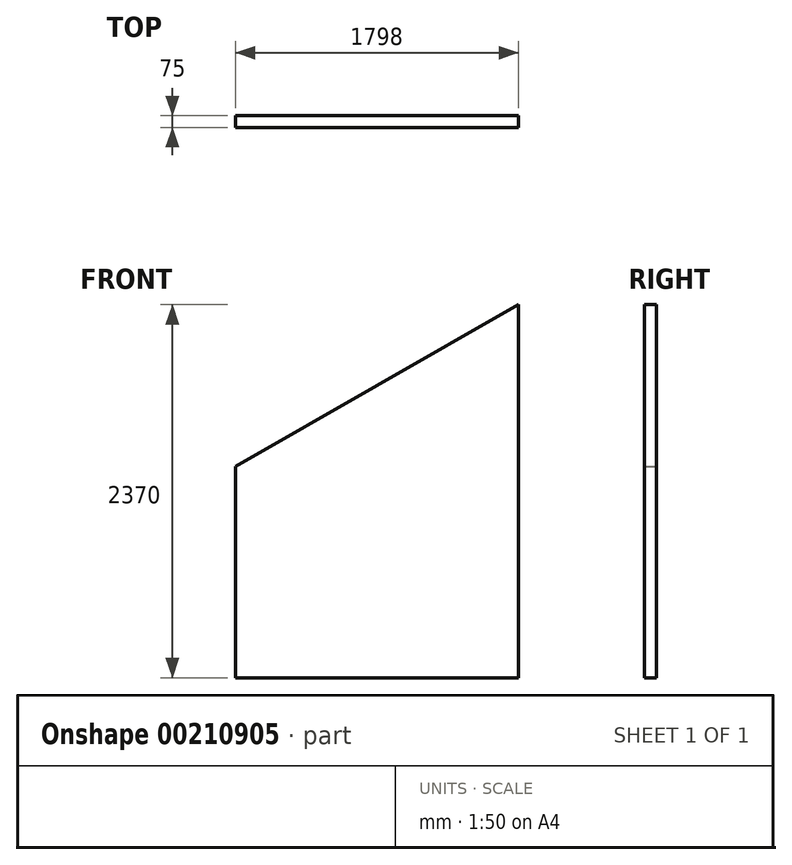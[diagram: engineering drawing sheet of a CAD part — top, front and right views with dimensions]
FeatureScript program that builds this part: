
annotation { "Feature Type Name" : "Feature", "Feature Type Description" : "" }
export const myFeature = defineFeature(function(context is Context, id is Id, definition is map)
    precondition{}
    {
        {
            var Q0;
            Q0=qCreatedBy(makeId("Front.planeOp"),FACE);
            var sketch = newSketch(context, id + "F0", { "sketchPlane" : qUnion([Q0])});
            skLineSegment(sketch, "E0.bottom", {"start": v(0, 0) * mm, "end": v(1798, 0) * mm});
            skLineSegment(sketch, "E0.right", {"start": v(1798, 0) * mm, "end": v(1798, 2370) * mm});
            skLineSegment(sketch, "E1", {"start": v(0, 0) * mm, "end": v(0, 1342) * mm});
            skLineSegment(sketch, "E2", {"start": v(0, 1342) * mm, "end": v(1798, 2370) * mm});
            skSolve(sketch);
        }
        {
            var Q0;
            Q0=makeQuery(id+"F0.imprint","IMPRINT",FACE,{"disambiguationData":[TD([[makeQuery(id+"F0.imprint","IMPRINT",EDGE,{"derivedFrom":sQuery(id+"F0.wireOp",EDGE,"E0.bottom")}),1.0]])]});
            extrude(context, id + "F1", {"entities" : qUnion([Q0]), "depth" : 75 * mm});
        }
    });
